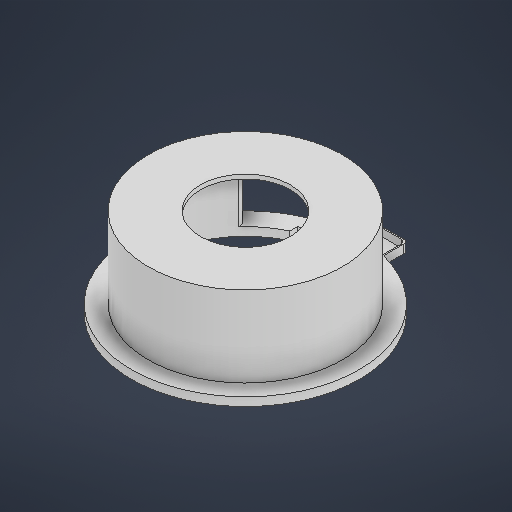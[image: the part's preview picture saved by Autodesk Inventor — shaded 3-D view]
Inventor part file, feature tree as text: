
AUTODESK INVENTOR PART (.ipt)
format: ipt  version: 2025 (Build 290162000, 162)  size: 327,168 bytes
history: native  units: in
note: dims shown in document units (in); Inventor stores cm internally (conversion verified against a paired STEP export)
features: extrude x7, sketch x3, fillet x2
ambient origin geometry x8: Origin, YZ Plane, XZ Plane, XY Plane, X Axis, Y Axis, Z Axis, Center Point
bodies: Solid1 (feature_tree)
feature tree (12):
  sketch  "Sketch1"  dims[d5=0.0in d7=0.0in]
  extrude  "Extrusion1"  TaperAngle=0.0deg  [1 undecoded]
  extrude  "Extrusion2"  Depth=4.5276in
  extrude  "Extrusion7"  Depth=2.5591in
  sketch  "Sketch24"  dims[d234=0.0787in d235=2.5591in d237=0.0591in d238=2.564in d240=0.8253in d241=10.6299in d242=2.7608in d243=0.5433in d244=1.5298in d247=0.0787in d248=3.5433in d249=3.6614in d250=0.0in d251=3.6614in d252=0.0in d253=9.4488in d254=0.3937in d255=0.0in d267=0.0394in d268=0.0in d274=0.1969in d275=0.0787in d113=0.0197in d114=0.0344in d115=0.0197in d116=0.0344in d167=0.0197in d168=0.0344in d169=0.0197in d170=0.0344in d215=0.0197in d216=0.0344in d217=0.0197in d218=0.0344in d219=0.0in d220=0.0in d256=0.0197in d257=0.0344in]
  extrude  "Extrusion30"  Depth=0.0591in
  extrude  "Extrusion31"  Depth=0.0787in
  extrude  "Extrusion32"  Depth=0.0787in
  extrude  "Extrusion35"  Depth=0.0787in
  fillet  "Fillet19"  Radius=2.7608in
  fillet  "Fillet20"  Radius=0.5433in
  sketch  "Sketch2"  dims[d18=0.0in d52=4.5276in]
note: 1 required parameter value undecoded (feature->parameter linkage not recoverable at this tier; creation-order binding heuristic only, values carry confidence <= 0.55)
